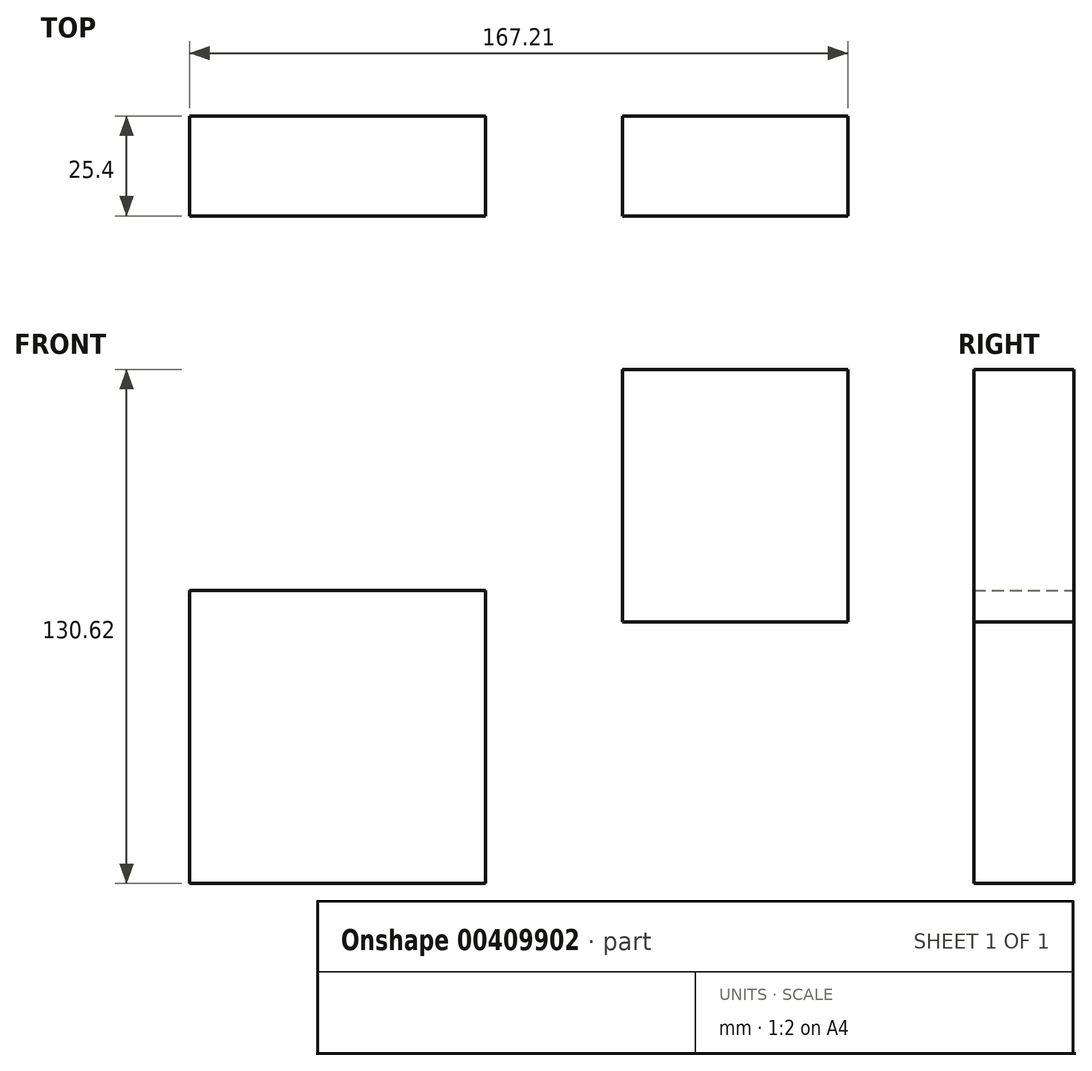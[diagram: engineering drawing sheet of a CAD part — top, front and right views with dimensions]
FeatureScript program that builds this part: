
annotation { "Feature Type Name" : "Feature", "Feature Type Description" : "" }
export const myFeature = defineFeature(function(context is Context, id is Id, definition is map)
    precondition{}
    {
        {
            var Q0;
            Q0=qCreatedBy(makeId("Front.planeOp"),FACE);
            var sketch = newSketch(context, id + "F0", { "sketchPlane" : qUnion([Q0])});
            skLineSegment(sketch, "E0.bottom", {"start": v(26.35, 74.44) * mm, "end": v(101.57, 74.44) * mm});
            skLineSegment(sketch, "E0.top", {"start": v(26.35, 0) * mm, "end": v(101.57, 0) * mm});
            skLineSegment(sketch, "E0.left", {"start": v(26.35, 74.44) * mm, "end": v(26.35, 0) * mm});
            skLineSegment(sketch, "E0.right", {"start": v(101.57, 74.44) * mm, "end": v(101.57, 0) * mm});
            skLineSegment(sketch, "E1.bottom", {"start": v(136.3, 130.62) * mm, "end": v(193.56, 130.62) * mm});
            skLineSegment(sketch, "E1.top", {"start": v(136.3, 66.42) * mm, "end": v(193.56, 66.42) * mm});
            skLineSegment(sketch, "E1.left", {"start": v(136.3, 130.62) * mm, "end": v(136.3, 66.42) * mm});
            skLineSegment(sketch, "E1.right", {"start": v(193.56, 130.62) * mm, "end": v(193.56, 66.42) * mm});
            skSolve(sketch);
        }
        {
            var Q0;
            Q0 = qSketchRegion(id + "F0", true);
            extrude(context, id + "F1", {"entities" : qUnion([Q0]), "depth" : 25.4 * mm});
        }
    });
